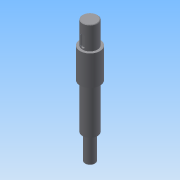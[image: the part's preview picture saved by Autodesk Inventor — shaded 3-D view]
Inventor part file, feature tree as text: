
AUTODESK INVENTOR PART (.ipt)
format: ipt  version: 2015 (Build 190159000, 159)  size: 131,584 bytes
history: native  units: mm
features: extrude x6, sketch x6, plane x2, chamfer x1
ambient origin geometry x8: Origin, YZ Plane, XZ Plane, XY Plane, X Axis, Y Axis, Z Axis, Center Point
bodies: 实体1 (feature_tree)
feature tree (15):
  extrude  "拉伸1"  Depth=51.0mm TaperAngle=0.0deg
  extrude  "拉伸2"  Depth=90.0mm TaperAngle=0.0deg
  extrude  "拉伸3"  Depth=60.0mm TaperAngle=0.0deg
  extrude  "拉伸4"  Depth=46.0mm TaperAngle=0.0deg
  chamfer  "倒角1"  Distance=1.0mm Angle=45.0deg
  plane  "工作平面1"
  extrude  "拉伸5"  Depth=6.187585mm
  plane  "工作平面2"
  extrude  "拉伸6"  Depth=8.0mm
  sketch  "草图1"  dims[d0=20.0mm d1=51.0mm d2=0.0mm]
  sketch  "草图2"  dims[d3=30.0mm d4=90.0mm d5=0.0mm]
  sketch  "草图3"  dims[d6=40.0mm d7=60.0mm d8=0.0mm]
  sketch  "草图4"  dims[d9=30.0mm d10=46.0mm d11=0.0mm d12=1.0mm d13=2.0mm d14=45.0deg]
  sketch  "草图5"  dims[d15=6.0mm d16=6.187585mm]
  sketch  "草图6"  dims[d17=6.5mm d18=22.0mm d19=2.5mm d20=0.0mm d21=6.5mm d22=8.0mm d23=17.0mm d24=3.0mm d25=0.0mm]
